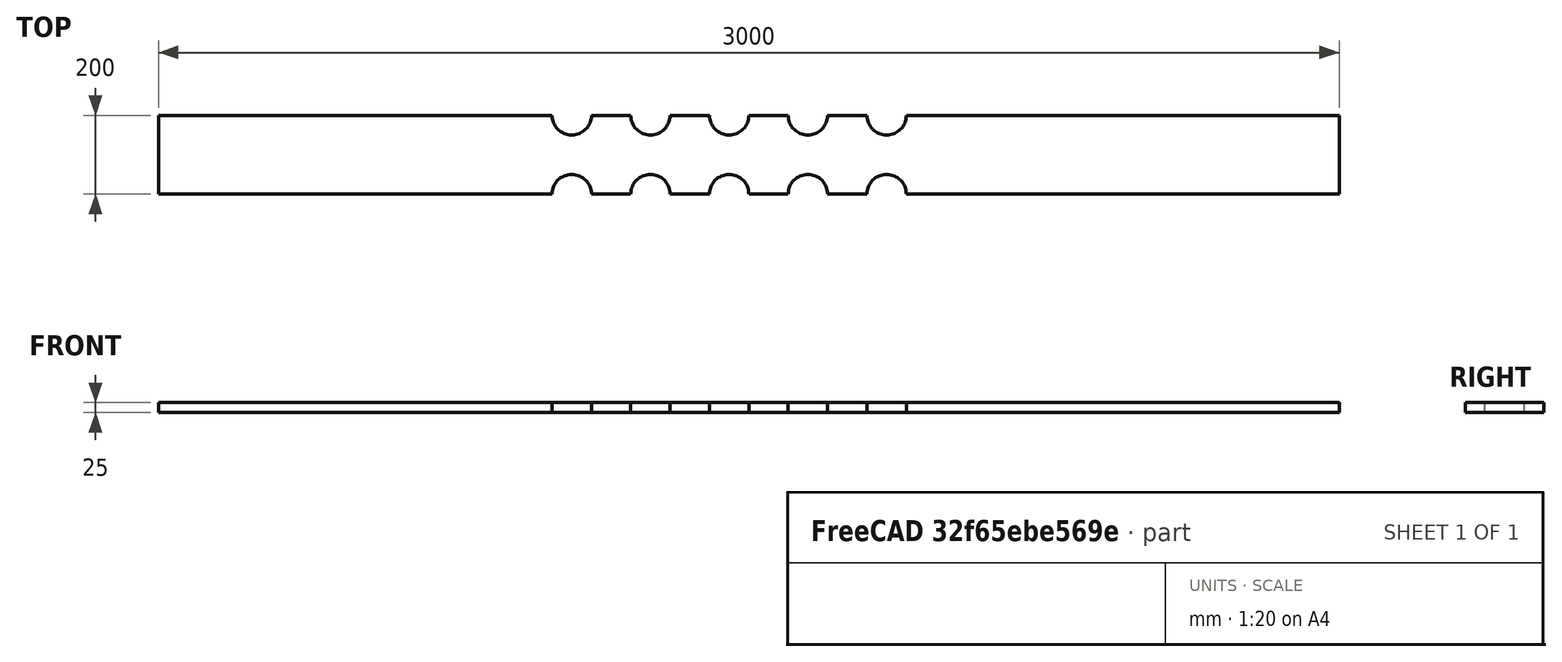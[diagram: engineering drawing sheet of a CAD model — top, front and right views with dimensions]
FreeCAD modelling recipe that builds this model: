
FCSTD DOCUMENT  (FreeCAD 0.17R10887 (Git))
Label: tubeBundlePressDropPart
License: All rights reserved
LicenseURL: http://en.wikipedia.org/wiki/All_rights_reserved
objects: Part::Cylinder×10, Part::Box×1, Part::MultiFuse×1, Part::Cut×1
note: 13 computed .brp shape members not serialized (recipe doc carries the construction recipe); baked Part::Feature solids carry a one-line shape summary decoded from their .brp

FEATURE [Part::Cylinder] Cylinder
  Angle = 360
  AttacherType = Attacher::AttachEngine3D
  Height = 25
  Placement = pos=(250,0,0) rot=(0,0,1;0rad)
  Radius = 50
FEATURE [Part::Box] Box  label="Cube"
  AttacherType = Attacher::AttachEngine3D
  Height = 25
  Length = 3000
  Placement = pos=(-800,0,0) rot=(0,0,1;0rad)
  Width = 200
FEATURE [Part::Cylinder] Cylinder001
  Angle = 360
  AttacherType = Attacher::AttachEngine3D
  Height = 25
  Placement = pos=(450,0,0) rot=(0,0,1;0rad)
  Radius = 50
FEATURE [Part::Cylinder] Cylinder002
  Angle = 360
  AttacherType = Attacher::AttachEngine3D
  Height = 25
  Placement = pos=(650,0,0) rot=(0,0,1;0rad)
  Radius = 50
FEATURE [Part::Cylinder] Cylinder003
  Angle = 360
  AttacherType = Attacher::AttachEngine3D
  Height = 25
  Placement = pos=(850,0,0) rot=(0,0,1;0rad)
  Radius = 50
FEATURE [Part::Cylinder] Cylinder004
  Angle = 360
  AttacherType = Attacher::AttachEngine3D
  Height = 25
  Placement = pos=(1050,0,0) rot=(0,0,1;0rad)
  Radius = 50
FEATURE [Part::Cylinder] Cylinder005
  Angle = 360
  AttacherType = Attacher::AttachEngine3D
  Height = 25
  Placement = pos=(250,200,0) rot=(0,0,1;0rad)
  Radius = 50
FEATURE [Part::Cylinder] Cylinder006
  Angle = 360
  AttacherType = Attacher::AttachEngine3D
  Height = 25
  Placement = pos=(450,200,0) rot=(0,0,1;0rad)
  Radius = 50
FEATURE [Part::Cylinder] Cylinder007
  Angle = 360
  AttacherType = Attacher::AttachEngine3D
  Height = 25
  Placement = pos=(650,200,0) rot=(0,0,1;0rad)
  Radius = 50
FEATURE [Part::Cylinder] Cylinder008
  Angle = 360
  AttacherType = Attacher::AttachEngine3D
  Height = 25
  Placement = pos=(850,200,0) rot=(0,0,1;0rad)
  Radius = 50
FEATURE [Part::Cylinder] Cylinder009
  Angle = 360
  AttacherType = Attacher::AttachEngine3D
  Height = 25
  Placement = pos=(1050,200,0) rot=(0,0,1;0rad)
  Radius = 50
FEATURE [Part::MultiFuse] Fusion
  Shapes = -> [Cylinder009,Cylinder,Cylinder002,Cylinder001,Cylinder003,Cylinder004,Cylinder006,Cylinder005,Cylinder007,Cylinder008]
FEATURE [Part::Cut] Cut
  Base = -> Box
  Tool = -> Fusion
